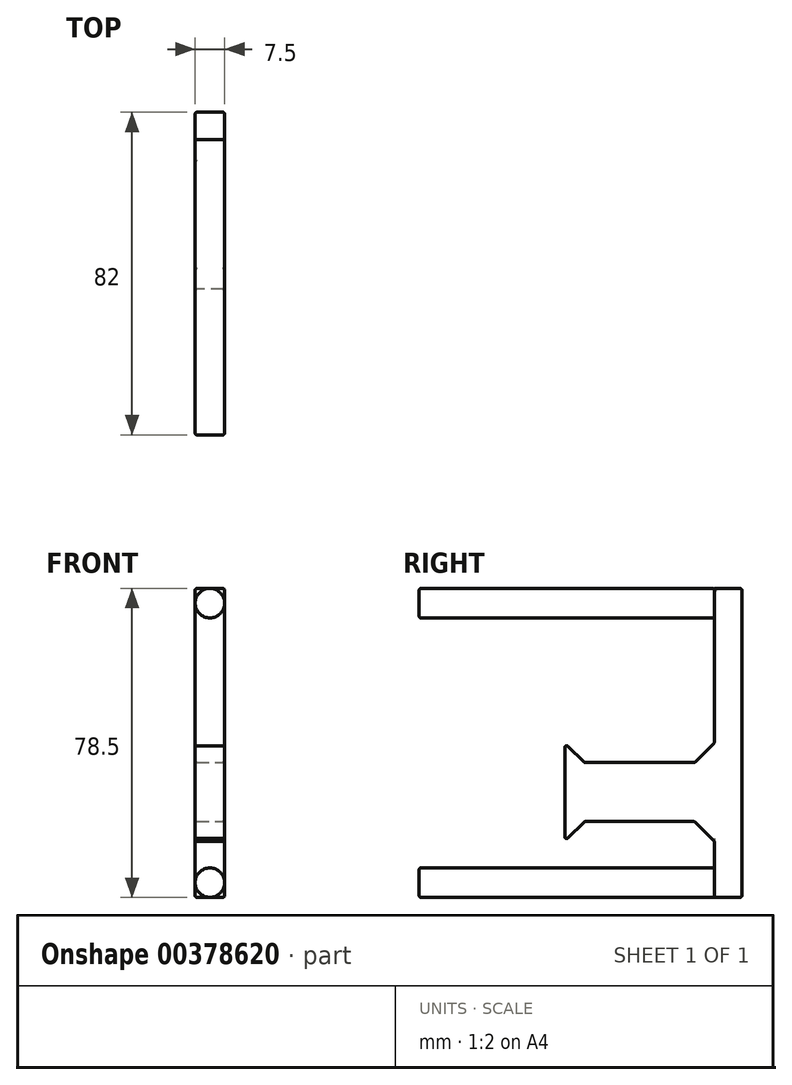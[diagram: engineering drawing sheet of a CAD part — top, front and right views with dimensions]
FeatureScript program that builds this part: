
annotation { "Feature Type Name" : "Feature", "Feature Type Description" : "" }
export const myFeature = defineFeature(function(context is Context, id is Id, definition is map)
    precondition{}
    {
        {
            var Q0;
            Q0=qCreatedBy(makeId("Front.planeOp"),FACE);
            var sketch = newSketch(context, id + "F0", { "sketchPlane" : qUnion([Q0])});
            skLineSegment(sketch, "E0", {"start": v(0, 35.5) * mm, "end": v(0, -35.5) * mm, "construction": true});
            skCircle(sketch, "E1", {"center": v(0, 35.5) * mm, "radius": 3.75 * mm});
            skCircle(sketch, "E2.MirrorC", {"center": v(0, -35.5) * mm, "radius": 3.75 * mm});
            skSolve(sketch);
        }
        {
            var Q0;
            Q0=qSketchRegion(id+"F0",true);
            extrude(context, id + "F1", {"entities" : qUnion([Q0]), "depth" : 75 * mm});
        }
        {
            var Q0;
            Q0=qCreatedBy(makeId("Front.planeOp"),FACE);
            var sketch = newSketch(context, id + "F2", { "sketchPlane" : qUnion([Q0])});
            skLineSegment(sketch, "E3.bottom", {"start": v(3.75, 39.25) * mm, "end": v(-3.75, 39.25) * mm});
            skLineSegment(sketch, "E3.top", {"start": v(3.75, -39.25) * mm, "end": v(-3.75, -39.25) * mm});
            skLineSegment(sketch, "E3.left", {"start": v(3.75, 39.25) * mm, "end": v(3.75, -39.25) * mm});
            skLineSegment(sketch, "E3.right", {"start": v(-3.75, 39.25) * mm, "end": v(-3.75, -39.25) * mm});
            skSolve(sketch);
        }
        {
            var Q0;
            Q0=qSketchRegion(id+"F2",true);
            extrude(context, id + "F3", {"entities" : qUnion([Q0]), "oppositeDirection" : true, "depth" : 7 * mm});
        }
        {
            var Q0;
            Q0=makeQuery(id+"F3.opExtrude","CAP_FACE",FACE,{"disambiguationData":[OSD([sQuery(id+"F2.wireOp",EDGE,"E3.bottom"),sQuery(id+"F2.wireOp",EDGE,"E3.top"),sQuery(id+"F2.wireOp",EDGE,"E3.left"),sQuery(id+"F2.wireOp",EDGE,"E3.right")])],"isStart":false});
            var sketch = newSketch(context, id + "F4", { "sketchPlane" : qUnion([Q0])});
            skLineSegment(sketch, "E4.bottom", {"start": v(-3.75, 0) * mm, "end": v(3.75, 0) * mm});
            skLineSegment(sketch, "E4.top", {"start": v(-3.75, -25) * mm, "end": v(3.75, -25) * mm});
            skLineSegment(sketch, "E4.left", {"start": v(-3.75, 0) * mm, "end": v(-3.75, -25) * mm});
            skLineSegment(sketch, "E4.right", {"start": v(3.75, 0) * mm, "end": v(3.75, -25) * mm});
            skSolve(sketch);
        }
        {
            var Q0;
            Q0=qSketchRegion(id+"F4",true);
            extrude(context, id + "F5", {"entities" : qUnion([Q0]), "operationType" : NewBodyOperationType.ADD, "oppositeDirection" : true, "depth" : 45 * mm});
        }
        {
            var Q0;
            Q0=makeQuery(id+"F5.boolean.opBoolean","MERGE",FACE,{"derivedFrom":[makeQuery(id+"F3.opExtrude","SWEPT_FACE",FACE,{"disambiguationData":[OSD([sQuery(id+"F2.wireOp",EDGE,"E3.left")])]}),makeQuery(id+"F5.opExtrude","SWEPT_FACE",FACE,{"disambiguationData":[OSD([sQuery(id+"F4.wireOp",EDGE,"E4.left")])]})]});
            var sketch = newSketch(context, id + "F6", { "sketchPlane" : qUnion([Q0])});
            skLineSegment(sketch, "E5", {"start": v(-38, 0) * mm, "end": v(-33, -5) * mm});
            skLineSegment(sketch, "E6", {"start": v(-33, -5) * mm, "end": v(-5, -5) * mm});
            skLineSegment(sketch, "E7", {"start": v(-5, -5) * mm, "end": v(0, 0) * mm});
            skLineSegment(sketch, "E8", {"start": v(-38, -12.5) * mm, "end": v(7, -12.5) * mm, "construction": true});
            skLineSegment(sketch, "E9.MirrorCS", {"start": v(-38, -25) * mm, "end": v(-33, -20) * mm});
            skLineSegment(sketch, "E10.MirrorCS", {"start": v(-33, -20) * mm, "end": v(-5, -20) * mm});
            skLineSegment(sketch, "E11.MirrorCS", {"start": v(-5, -20) * mm, "end": v(0, -25) * mm});
            skLineSegment(sketch, "E12", {"start": v(-38, 0) * mm, "end": v(0, 0) * mm});
            skLineSegment(sketch, "E13", {"start": v(0, -25) * mm, "end": v(-38, -25) * mm});
            skSolve(sketch);
        }
        {
            var Q0;
            Q0=qSketchRegion(id+"F6",true);
            var Q1;
            Q1=makeQuery(id+"F5.boolean.opBoolean","MERGE",FACE,{"derivedFrom":[makeQuery(id+"F3.opExtrude","SWEPT_FACE",FACE,{"disambiguationData":[OSD([sQuery(id+"F2.wireOp",EDGE,"E3.right")])]}),makeQuery(id+"F5.opExtrude","SWEPT_FACE",FACE,{"disambiguationData":[OSD([sQuery(id+"F4.wireOp",EDGE,"E4.right")])]})]});
            extrude(context, id + "F7", {"entities" : qUnion([Q0]), "operationType" : NewBodyOperationType.REMOVE, "oppositeDirection" : true, "endBoundEntityFace" : qUnion([Q1]), "depth" : 25 * mm});
        }
        {
            var Q0;
            Q0=makeQuery(id+"FCb6eM4hjmSESD8_3.boolean.opBoolean","COPY",EDGE,{"derivedFrom":makeQuery(id+"FCb6eM4hjmSESD8_3.opExtrude","SWEPT_EDGE",EDGE,{"disambiguationData":[OSD([sQuery(id+"FaSfIvEzDDoyCTc_3.wireOp",EDGE,"4808a14a-dd14-42e4-b01e-38bb08252985.2"),sQuery(id+"FaSfIvEzDDoyCTc_3.wireOp",EDGE,"4808a14a-dd14-42e4-b01e-38bb08252985.3")])]})});
            var Q1;
            Q1=makeQuery(id+"FCb6eM4hjmSESD8_3.boolean.opBoolean","COPY",EDGE,{"derivedFrom":makeQuery(id+"FCb6eM4hjmSESD8_3.opExtrude","SWEPT_EDGE",EDGE,{"disambiguationData":[OSD([sQuery(id+"FaSfIvEzDDoyCTc_3.wireOp",EDGE,"4808a14a-dd14-42e4-b01e-38bb08252985.1"),sQuery(id+"FaSfIvEzDDoyCTc_3.wireOp",EDGE,"4808a14a-dd14-42e4-b01e-38bb08252985.2")])]})});
            var Q2;
            Q2=makeQuery(id+"FCb6eM4hjmSESD8_3.boolean.opBoolean","COPY",EDGE,{"derivedFrom":makeQuery(id+"FCb6eM4hjmSESD8_3.opExtrude","SWEPT_EDGE",EDGE,{"disambiguationData":[OSD([sQuery(id+"FaSfIvEzDDoyCTc_3.wireOp",EDGE,"4808a14a-dd14-42e4-b01e-38bb08252985.0"),sQuery(id+"FaSfIvEzDDoyCTc_3.wireOp",EDGE,"4808a14a-dd14-42e4-b01e-38bb08252985.3")])]})});
            var Q3;
            Q3=makeQuery(id+"F3.opExtrude","SWEPT_EDGE",EDGE,{"disambiguationData":[OSD([sQuery(id+"F2.wireOp",EDGE,"E3.top"),sQuery(id+"F2.wireOp",EDGE,"E3.right")])]});
            var Q4;
            Q4=makeQuery(id+"F3.opExtrude","CAP_EDGE",EDGE,{"disambiguationData":[OSD([sQuery(id+"F2.wireOp",EDGE,"E3.top")])],"isStart":false});
            var Q5;
            Q5=makeQuery(id+"F3.opExtrude","SWEPT_EDGE",EDGE,{"disambiguationData":[OSD([sQuery(id+"F2.wireOp",EDGE,"E3.top"),sQuery(id+"F2.wireOp",EDGE,"E3.left")])]});
            var Q6;
            {var subQ0=sQuery(id+"F2.wireOp",EDGE,"E3.right");var subQ1=sQuery(id+"F2.wireOp",EDGE,"E3.top");Q6=makeQuery(id+"FioXNadC86z8tVF_3.boolean.opBoolean","SPLIT",EDGE,{"disambiguationData":[TD([makeQuery(id+"F3.opExtrude","SWEPT_FACE",FACE,{"disambiguationData":[OSD([subQ1])]})])],"derivedFrom":makeQuery(id+"F3.opExtrude","CAP_EDGE",EDGE,{"disambiguationData":[OSD([subQ0])],"isStart":false})});}
            var Q7;
            Q7=makeQuery(id+"F3.opExtrude","CAP_EDGE",EDGE,{"disambiguationData":[OSD([sQuery(id+"F2.wireOp",EDGE,"E3.left")])],"isStart":false});
            var Q8;
            Q8=makeQuery(id+"FioXNadC86z8tVF_3.opExtrude","SWEPT_EDGE",EDGE,{"disambiguationData":[OSD([sQuery(id+"F2.wireOp",EDGE,"E3.right"),sQuery(id+"Fk22kIUswROca2C_3.wireOp",EDGE,"bvUl3gom-Cpna-lFYu-iHQ9-kMqEEKe5kjJ8.top"),sQuery(id+"Fk22kIUswROca2C_3.wireOp",EDGE,"bvUl3gom-Cpna-lFYu-iHQ9-kMqEEKe5kjJ8.left")])]});
            var Q9;
            Q9=makeQuery(id+"FioXNadC86z8tVF_3.opExtrude","SWEPT_EDGE",EDGE,{"disambiguationData":[OSD([sQuery(id+"F2.wireOp",EDGE,"E3.right"),sQuery(id+"Fk22kIUswROca2C_3.wireOp",EDGE,"bvUl3gom-Cpna-lFYu-iHQ9-kMqEEKe5kjJ8.bottom"),sQuery(id+"Fk22kIUswROca2C_3.wireOp",EDGE,"bvUl3gom-Cpna-lFYu-iHQ9-kMqEEKe5kjJ8.left")])]});
            var Q10;
            {var subQ0=sQuery(id+"F2.wireOp",EDGE,"E3.right");var subQ1=sQuery(id+"F2.wireOp",EDGE,"E3.bottom");Q10=makeQuery(id+"FioXNadC86z8tVF_3.boolean.opBoolean","SPLIT",EDGE,{"disambiguationData":[TD([makeQuery(id+"F3.opExtrude","SWEPT_FACE",FACE,{"disambiguationData":[OSD([subQ1])]})])],"derivedFrom":makeQuery(id+"F3.opExtrude","CAP_EDGE",EDGE,{"disambiguationData":[OSD([subQ0])],"isStart":false})});}
            var Q11;
            Q11=makeQuery(id+"F7.boolean.opBoolean","COPY",EDGE,{"derivedFrom":makeQuery(id+"F7.opExtrude","CAP_EDGE",EDGE,{"disambiguationData":[OSD([sQuery(id+"F6.wireOp",EDGE,"E10.MirrorCS")])],"isStart":true})});
            var Q12;
            Q12=makeQuery(id+"F7.boolean.opBoolean","COPY",EDGE,{"derivedFrom":makeQuery(id+"F7.opExtrude","CAP_EDGE",EDGE,{"disambiguationData":[OSD([sQuery(id+"F6.wireOp",EDGE,"E11.MirrorCS")])],"isStart":true})});
            var Q13;
            Q13=makeQuery(id+"F7.boolean.opBoolean","INTERSECT",EDGE,{"derivedFrom":[makeQuery(id+"F5.boolean.opBoolean","MERGE",FACE,{"derivedFrom":[makeQuery(id+"F3.opExtrude","SWEPT_FACE",FACE,{"disambiguationData":[OSD([sQuery(id+"F2.wireOp",EDGE,"E3.right")])]}),makeQuery(id+"F5.opExtrude","SWEPT_FACE",FACE,{"disambiguationData":[OSD([sQuery(id+"F4.wireOp",EDGE,"E4.right")])]})]}),makeQuery(id+"F7.opExtrude","SWEPT_FACE",FACE,{"disambiguationData":[OSD([sQuery(id+"F6.wireOp",EDGE,"E11.MirrorCS")])]})]});
            var Q14;
            Q14=makeQuery(id+"F7.boolean.opBoolean","INTERSECT",EDGE,{"derivedFrom":[makeQuery(id+"F5.boolean.opBoolean","MERGE",FACE,{"derivedFrom":[makeQuery(id+"F3.opExtrude","SWEPT_FACE",FACE,{"disambiguationData":[OSD([sQuery(id+"F2.wireOp",EDGE,"E3.right")])]}),makeQuery(id+"F5.opExtrude","SWEPT_FACE",FACE,{"disambiguationData":[OSD([sQuery(id+"F4.wireOp",EDGE,"E4.right")])]})]}),makeQuery(id+"F7.opExtrude","SWEPT_FACE",FACE,{"disambiguationData":[OSD([sQuery(id+"F6.wireOp",EDGE,"E10.MirrorCS")])]})]});
            var Q15;
            Q15=makeQuery(id+"F7.boolean.opBoolean","COPY",EDGE,{"derivedFrom":makeQuery(id+"F7.opExtrude","SWEPT_EDGE",EDGE,{"disambiguationData":[OSD([sQuery(id+"F6.wireOp",EDGE,"E10.MirrorCS"),sQuery(id+"F6.wireOp",EDGE,"E11.MirrorCS")])]})});
            var Q16;
            {var subQ0=sQuery(id+"F2.wireOp",EDGE,"E3.left");Q16=makeQuery(id+"F7.boolean.opBoolean","MERGE",EDGE,{"derivedFrom":[makeQuery(id+"F5.boolean.opBoolean","INTERSECT",EDGE,{"derivedFrom":[makeQuery(id+"F3.opExtrude","CAP_FACE",FACE,{"disambiguationData":[OSD([sQuery(id+"F2.wireOp",EDGE,"E3.bottom"),sQuery(id+"F2.wireOp",EDGE,"E3.top"),subQ0,sQuery(id+"F2.wireOp",EDGE,"E3.right")])],"isStart":true}),makeQuery(id+"F5.opExtrude","SWEPT_FACE",FACE,{"disambiguationData":[OSD([sQuery(id+"F4.wireOp",EDGE,"E4.bottom")])]})]}),makeQuery(id+"F7.opExtrude","SWEPT_EDGE",EDGE,{"disambiguationData":[OSD([subQ0,sQuery(id+"F6.wireOp",EDGE,"E7"),sQuery(id+"F6.wireOp",EDGE,"E12")])]})]});}
            var Q17;
            Q17=makeQuery(id+"F7.boolean.opBoolean","COPY",EDGE,{"derivedFrom":makeQuery(id+"F7.opExtrude","SWEPT_EDGE",EDGE,{"disambiguationData":[OSD([sQuery(id+"F6.wireOp",EDGE,"E6"),sQuery(id+"F6.wireOp",EDGE,"E7")])]})});
            var Q18;
            Q18=makeQuery(id+"F7.boolean.opBoolean","COPY",EDGE,{"derivedFrom":makeQuery(id+"F7.opExtrude","CAP_EDGE",EDGE,{"disambiguationData":[OSD([sQuery(id+"F6.wireOp",EDGE,"E7")])],"isStart":true})});
            var Q19;
            Q19=makeQuery(id+"F7.boolean.opBoolean","COPY",EDGE,{"derivedFrom":makeQuery(id+"F7.opExtrude","CAP_EDGE",EDGE,{"disambiguationData":[OSD([sQuery(id+"F6.wireOp",EDGE,"E6")])],"isStart":true})});
            var Q20;
            Q20=makeQuery(id+"F7.boolean.opBoolean","INTERSECT",EDGE,{"derivedFrom":[makeQuery(id+"F5.boolean.opBoolean","MERGE",FACE,{"derivedFrom":[makeQuery(id+"F3.opExtrude","SWEPT_FACE",FACE,{"disambiguationData":[OSD([sQuery(id+"F2.wireOp",EDGE,"E3.right")])]}),makeQuery(id+"F5.opExtrude","SWEPT_FACE",FACE,{"disambiguationData":[OSD([sQuery(id+"F4.wireOp",EDGE,"E4.right")])]})]}),makeQuery(id+"F7.opExtrude","SWEPT_FACE",FACE,{"disambiguationData":[OSD([sQuery(id+"F6.wireOp",EDGE,"E7")])]})]});
            var Q21;
            {var subQ0=sQuery(id+"F2.wireOp",EDGE,"E3.right");var subQ1=sQuery(id+"F2.wireOp",EDGE,"E3.bottom");Q21=makeQuery(id+"F5.boolean.opBoolean","SPLIT",EDGE,{"disambiguationData":[TD([makeQuery(id+"F3.opExtrude","SWEPT_FACE",FACE,{"disambiguationData":[OSD([subQ1])]})])],"derivedFrom":makeQuery(id+"F3.opExtrude","CAP_EDGE",EDGE,{"disambiguationData":[OSD([subQ0])],"isStart":true})});}
            var Q22;
            Q22=makeQuery(id+"F7.boolean.opBoolean","INTERSECT",EDGE,{"derivedFrom":[makeQuery(id+"F5.boolean.opBoolean","MERGE",FACE,{"derivedFrom":[makeQuery(id+"F3.opExtrude","SWEPT_FACE",FACE,{"disambiguationData":[OSD([sQuery(id+"F2.wireOp",EDGE,"E3.right")])]}),makeQuery(id+"F5.opExtrude","SWEPT_FACE",FACE,{"disambiguationData":[OSD([sQuery(id+"F4.wireOp",EDGE,"E4.right")])]})]}),makeQuery(id+"F7.opExtrude","SWEPT_FACE",FACE,{"disambiguationData":[OSD([sQuery(id+"F6.wireOp",EDGE,"E5")])]})]});
            var Q23;
            Q23=makeQuery(id+"FioXNadC86z8tVF_3.opExtrude","SWEPT_FACE",FACE,{"disambiguationData":[OSD([sQuery(id+"Fk22kIUswROca2C_3.wireOp",EDGE,"bvUl3gom-Cpna-lFYu-iHQ9-kMqEEKe5kjJ8.right")])]});
            var Q24;
            Q24=makeQuery(id+"F3.opExtrude","CAP_EDGE",EDGE,{"disambiguationData":[OSD([sQuery(id+"F2.wireOp",EDGE,"E3.bottom")])],"isStart":false});
            var Q25;
            Q25=makeQuery(id+"F3.opExtrude","SWEPT_EDGE",EDGE,{"disambiguationData":[OSD([sQuery(id+"F2.wireOp",EDGE,"E3.bottom"),sQuery(id+"F2.wireOp",EDGE,"E3.left")])]});
            var Q26;
            Q26=makeQuery(id+"F3.opExtrude","SWEPT_EDGE",EDGE,{"disambiguationData":[OSD([sQuery(id+"F2.wireOp",EDGE,"E3.bottom"),sQuery(id+"F2.wireOp",EDGE,"E3.right")])]});
            var Q27;
            Q27=makeQuery(id+"F7.boolean.opBoolean","MERGE",EDGE,{"derivedFrom":[makeQuery(id+"F5.opExtrude","CAP_EDGE",EDGE,{"disambiguationData":[OSD([sQuery(id+"F4.wireOp",EDGE,"E4.top")])],"isStart":false}),makeQuery(id+"F7.opExtrude","SWEPT_EDGE",EDGE,{"disambiguationData":[OSD([sQuery(id+"F4.wireOp",EDGE,"E4.left"),sQuery(id+"F6.wireOp",EDGE,"E9.MirrorCS"),sQuery(id+"F6.wireOp",EDGE,"E13")])]})]});
            var Q28;
            Q28=makeQuery(id+"F5.opExtrude","CAP_FACE",FACE,{"disambiguationData":[OSD([sQuery(id+"F4.wireOp",EDGE,"E4.bottom"),sQuery(id+"F4.wireOp",EDGE,"E4.top"),sQuery(id+"F4.wireOp",EDGE,"E4.left"),sQuery(id+"F4.wireOp",EDGE,"E4.right")])],"isStart":false});
            var Q29;
            Q29=makeQuery(id+"F7.boolean.opBoolean","COPY",FACE,{"derivedFrom":makeQuery(id+"F7.opExtrude","SWEPT_FACE",FACE,{"disambiguationData":[OSD([sQuery(id+"F6.wireOp",EDGE,"E9.MirrorCS")])]})});
            var Q30;
            Q30=makeQuery(id+"F7.boolean.opBoolean","COPY",FACE,{"derivedFrom":makeQuery(id+"F7.opExtrude","SWEPT_FACE",FACE,{"disambiguationData":[OSD([sQuery(id+"F6.wireOp",EDGE,"E5")])]})});
            var Q31;
            Q31=makeQuery(id+"FioXNadC86z8tVF_3.opExtrude","CAP_FACE",FACE,{"disambiguationData":[OSD([sQuery(id+"Fk22kIUswROca2C_3.wireOp",EDGE,"bvUl3gom-Cpna-lFYu-iHQ9-kMqEEKe5kjJ8.bottom"),sQuery(id+"Fk22kIUswROca2C_3.wireOp",EDGE,"bvUl3gom-Cpna-lFYu-iHQ9-kMqEEKe5kjJ8.top"),sQuery(id+"Fk22kIUswROca2C_3.wireOp",EDGE,"bvUl3gom-Cpna-lFYu-iHQ9-kMqEEKe5kjJ8.left"),sQuery(id+"Fk22kIUswROca2C_3.wireOp",EDGE,"bvUl3gom-Cpna-lFYu-iHQ9-kMqEEKe5kjJ8.right")])],"isStart":false});
            var Q32;
            Q32=makeQuery(id+"FCb6eM4hjmSESD8_3.boolean.opBoolean","COPY",FACE,{"derivedFrom":makeQuery(id+"FCb6eM4hjmSESD8_3.opExtrude","SWEPT_FACE",FACE,{"disambiguationData":[OSD([sQuery(id+"FaSfIvEzDDoyCTc_3.wireOp",EDGE,"4808a14a-dd14-42e4-b01e-38bb08252985.2")])]})});
            var Q33;
            Q33=makeQuery(id+"FCb6eM4hjmSESD8_3.boolean.opBoolean","COPY",FACE,{"derivedFrom":makeQuery(id+"FCb6eM4hjmSESD8_3.opExtrude","SWEPT_FACE",FACE,{"disambiguationData":[OSD([sQuery(id+"FaSfIvEzDDoyCTc_3.wireOp",EDGE,"4808a14a-dd14-42e4-b01e-38bb08252985.1")])]})});
            var Q34;
            Q34=makeQuery(id+"F1.opExtrude","CAP_EDGE",EDGE,{"disambiguationData":[OSD([sQuery(id+"F0.wireOp",EDGE,"E2.MirrorC")])],"isStart":false});
            var Q35;
            Q35=makeQuery(id+"F1.opExtrude","CAP_EDGE",EDGE,{"disambiguationData":[OSD([sQuery(id+"F0.wireOp",EDGE,"E1")])],"isStart":false});
            var Q36;
            Q36=makeQuery(id+"F1.opExtrude","SWEPT_FACE",FACE,{"disambiguationData":[OSD([sQuery(id+"F0.wireOp",EDGE,"E1")])]});
            fillet(context, id + "F8", {"entities" : qUnion([Q0, Q1, Q2, Q3, Q4, Q5, Q6, Q7, Q8, Q9, Q10, Q11, Q12, Q13, Q14, Q15, Q16, Q17, Q18, Q19, Q20, Q21, Q22, Q23, Q24, Q25, Q26, Q27, Q28, Q29, Q30, Q31, Q32, Q33, Q34, Q35, Q36]), "radius" : 0.5 * mm, "tangentPropagation" : true, "allowEdgeOverflow" : false});
        }
    });
